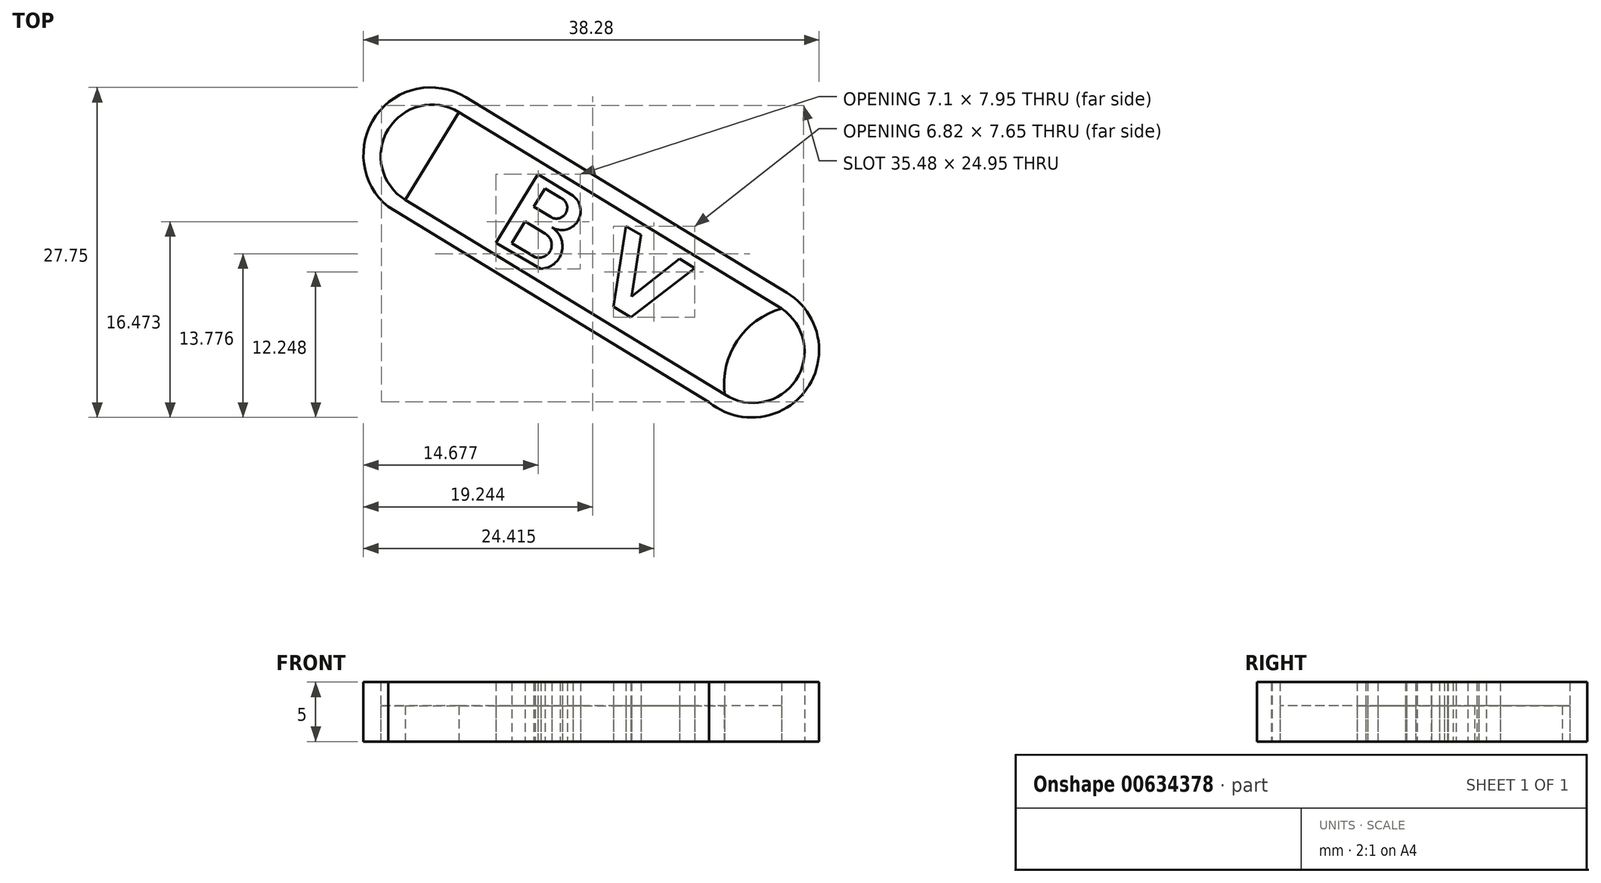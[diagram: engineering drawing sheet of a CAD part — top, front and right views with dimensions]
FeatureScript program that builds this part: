
annotation { "Feature Type Name" : "Feature", "Feature Type Description" : "" }
export const myFeature = defineFeature(function(context is Context, id is Id, definition is map)
    precondition{}
    {
        {
            var Q0;
            Q0=qCreatedBy(makeId("Top.planeOp"),FACE);
            var sketch = newSketch(context, id + "F0", { "sketchPlane" : qUnion([Q0])});
            skArc(sketch, "E0", {"start": v(-28.84, 9.2) * mm, "mid": v(-36.4, 7.65) * mm, "end": v(-35.37, 0) * mm});
            skLineSegment(sketch, "E1", {"start": v(-28.84, 9.2) * mm, "end": v(-1.87, -7.23) * mm});
            skLineSegment(sketch, "E2", {"start": v(-35.37, 0) * mm, "end": v(-8.4, -16.44) * mm});
            skArc(sketch, "E3", {"start": v(-8.4, -16.44) * mm, "mid": v(-0.2, -15.33) * mm, "end": v(-1.87, -7.23) * mm});
            skArc(sketch, "E4", {"start": v(-7.09, -15.78) * mm, "mid": v(-1.1, -14.56) * mm, "end": v(-2.31, -8.57) * mm});
            skArc(sketch, "E5", {"start": v(-2.31, -8.57) * mm, "mid": v(-6.05, -11.28) * mm, "end": v(-7.09, -15.78) * mm});
            skLineSegment(sketch, "E6", {"start": v(-2.31, -8.57) * mm, "end": v(-29.42, 7.95) * mm});
            skLineSegment(sketch, "E7", {"start": v(-29.42, 7.95) * mm, "end": v(-33.92, 0.57) * mm});
            skLineSegment(sketch, "E8", {"start": v(-33.92, 0.57) * mm, "end": v(-7.09, -15.78) * mm});
            skArc(sketch, "E9", {"start": v(-29.42, 7.95) * mm, "mid": v(-35.36, 6.51) * mm, "end": v(-33.92, 0.57) * mm});
            skLineSegment(sketch, "E10", {"start": v(-15.38, -1.64) * mm, "end": v(-16.43, -8.4) * mm});
            skLineSegment(sketch, "E11", {"start": v(-16.43, -8.4) * mm, "end": v(-14.96, -9.3) * mm});
            skLineSegment(sketch, "E12", {"start": v(-14.96, -9.3) * mm, "end": v(-9.61, -5.15) * mm});
            skLineSegment(sketch, "E13", {"start": v(-9.61, -5.15) * mm, "end": v(-10.9, -4.37) * mm});
            skLineSegment(sketch, "E14", {"start": v(-10.9, -4.37) * mm, "end": v(-14.91, -7.54) * mm});
            skLineSegment(sketch, "E15", {"start": v(-14.91, -7.54) * mm, "end": v(-14.1, -2.38) * mm});
            skLineSegment(sketch, "E16", {"start": v(-14.1, -2.38) * mm, "end": v(-15.38, -1.64) * mm});
            skLineSegment(sketch, "E17", {"start": v(-22.8, 2.73) * mm, "end": v(-26.31, -3.05) * mm});
            skLineSegment(sketch, "E18", {"start": v(-26.31, -3.05) * mm, "end": v(-22.53, -5.22) * mm});
            skLineSegment(sketch, "E19", {"start": v(-22.8, 2.73) * mm, "end": v(-19.84, 0.93) * mm});
            skLineSegment(sketch, "E20", {"start": v(-24.45, 0) * mm, "end": v(-21.62, -1.72) * mm});
            skArc(sketch, "E21", {"start": v(-21.62, -1.72) * mm, "mid": v(-19.46, -1.25) * mm, "end": v(-19.84, 0.93) * mm});
            skArc(sketch, "E22", {"start": v(-22.53, -5.22) * mm, "mid": v(-20.78, -3.8) * mm, "end": v(-21.62, -1.72) * mm});
            skLineSegment(sketch, "E23", {"start": v(-23.12, 0) * mm, "end": v(-22.18, 1.55) * mm});
            skLineSegment(sketch, "E24", {"start": v(-22.18, 1.55) * mm, "end": v(-20.9, 0.77) * mm});
            skLineSegment(sketch, "E25", {"start": v(-23.12, 0) * mm, "end": v(-21.7, -0.86) * mm});
            skPoint(sketch, "E25.endSnap0", {"position": v(-23.04, -0.86) * mm});
            skArc(sketch, "E26", {"start": v(-21.7, -0.86) * mm, "mid": v(-20.41, -0.49) * mm, "end": v(-20.9, 0.77) * mm});
            skLineSegment(sketch, "E27", {"start": v(-23.85, -1.23) * mm, "end": v(-24.97, -3.06) * mm});
            skLineSegment(sketch, "E28", {"start": v(-24.97, -3.06) * mm, "end": v(-23.02, -4.25) * mm});
            skLineSegment(sketch, "E29", {"start": v(-23.85, -1.23) * mm, "end": v(-22.15, -2.27) * mm});
            skArc(sketch, "E30", {"start": v(-23.02, -4.25) * mm, "mid": v(-21.72, -3.64) * mm, "end": v(-22.15, -2.27) * mm});
            skSolve(sketch);
        }
        {
            var Q0;
            Q0=makeQuery(id+"F0.imprint","IMPRINT",FACE,{"disambiguationData":[TD([[makeQuery(id+"F0.imprint","IMPRINT",EDGE,{"derivedFrom":sQuery(id+"F0.wireOp",EDGE,"E0")}),1.0]])]});
            var Q1;
            {var subQ1=sQuery(id+"F0.wireOp",EDGE,"E19");Q1=makeQuery(id+"F0.imprint","IMPRINT",FACE,{"disambiguationData":[TD([[makeQuery(id+"F0.imprint","IMPRINT",EDGE,{"derivedFrom":subQ1}),-1.0]])]});}
            var Q2;
            {var subQ1=sQuery(id+"F0.wireOp",EDGE,"E18");Q2=makeQuery(id+"F0.imprint","IMPRINT",FACE,{"disambiguationData":[TD([[makeQuery(id+"F0.imprint","IMPRINT",EDGE,{"derivedFrom":subQ1}),1.0]])]});}
            var Q3;
            Q3=makeQuery(id+"F0.imprint","IMPRINT",FACE,{"disambiguationData":[TD([[makeQuery(id+"F0.imprint","IMPRINT",EDGE,{"derivedFrom":sQuery(id+"F0.wireOp",EDGE,"E10")}),1.0]])]});
            extrude(context, id + "F1", {"entities" : qUnion([Q0, Q1, Q2, Q3]), "depth" : 5 * mm, "offsetDistance" : 25 * mm});
        }
        {
            var Q0;
            Q0=makeQuery(id+"F0.imprint","IMPRINT",FACE,{"disambiguationData":[TD([[makeQuery(id+"F0.imprint","IMPRINT",EDGE,{"derivedFrom":sQuery(id+"F0.wireOp",EDGE,"E5")}),-1.0]])]});
            extrude(context, id + "F2", {"entities" : qUnion([Q0]), "depth" : 3 * mm, "offsetDistance" : 25 * mm});
        }
        {
            var Q0;
            Q0=makeQuery(id+"F0.imprint","IMPRINT",FACE,{"disambiguationData":[TD([[makeQuery(id+"F0.imprint","IMPRINT",EDGE,{"derivedFrom":sQuery(id+"F0.wireOp",EDGE,"E7")}),-1.0]])]});
            extrude(context, id + "F3", {"entities" : qUnion([Q0]), "depth" : 3 * mm, "offsetDistance" : 25 * mm});
        }
    });
